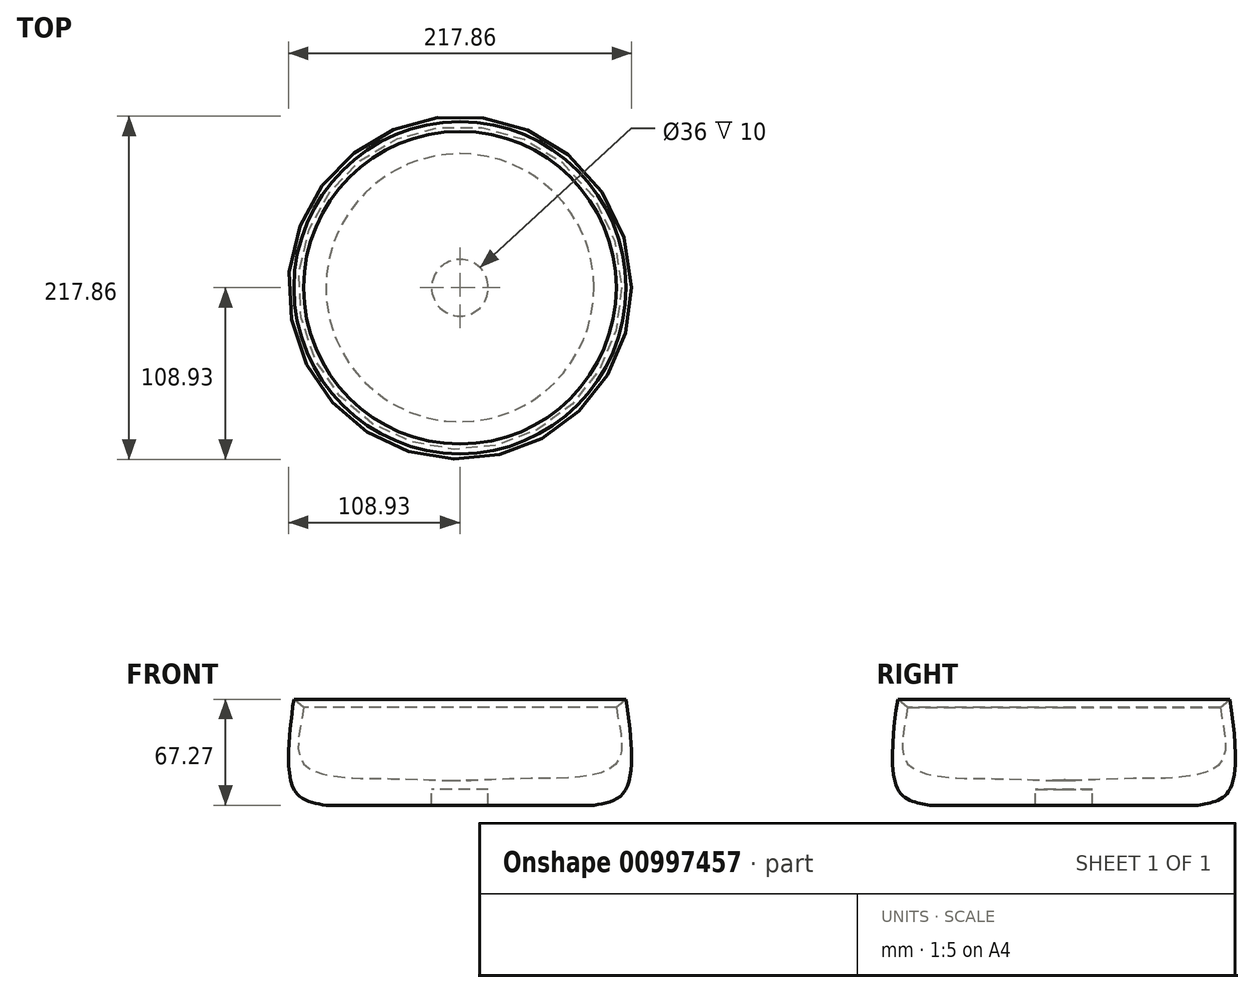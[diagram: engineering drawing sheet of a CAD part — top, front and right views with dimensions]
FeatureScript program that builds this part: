
annotation { "Feature Type Name" : "Feature", "Feature Type Description" : "" }
export const myFeature = defineFeature(function(context is Context, id is Id, definition is map)
    precondition{}
    {
        {
            var Q0;
            Q0=qCreatedBy(makeId("Front.planeOp"),FACE);
            var sketch = newSketch(context, id + "F0", { "sketchPlane" : qUnion([Q0])});
            skLineSegment(sketch, "E0.top", {"start": v(0, 10) * mm, "end": v(18, 10) * mm});
            skLineSegment(sketch, "E0.right", {"start": v(18, 0) * mm, "end": v(18, 10) * mm});
            skLineSegment(sketch, "E1", {"start": v(18, 0) * mm, "end": v(85.12, 0) * mm});
            skFitSpline(sketch, "E2", {"points": [v(85.12, 0) * mm, v(104.67, 8.92) * mm, v(105.46, 67.27) * mm], "startDerivative": vector(59.85, 10.55) * mm, "endDerivative": vector(-15.83, 104.7) * mm});
            skLineSegment(sketch, "E3", {"start": v(0, 16) * mm, "end": v(0, 10) * mm});
            skLineSegment(sketch, "E4", {"start": v(105.46, 67.27) * mm, "end": v(99.29, 62.18) * mm});
            skFitSpline(sketch, "E5", {"points": [v(99.29, 62.18) * mm, v(99.29, 26.49) * mm, v(39.52, 16.85) * mm, v(0, 16) * mm], "startDerivative": vector(15.04, -123.43) * mm, "endDerivative": vector(-113.7, 6.48) * mm});
            skSolve(sketch);
        }
        {
            var Q0;
            Q0=makeQuery(id+"F0.imprint","IMPRINT",FACE,{"disambiguationData":[TD([[makeQuery(id+"F0.imprint","IMPRINT",EDGE,{"derivedFrom":sQuery(id+"F0.wireOp",EDGE,"E0.top")}),1.0]])]});
            var Q1;
            Q1=sQuery(id+"F0.wireOp",EDGE,"E3");
            revolve(context, id + "F1", {"surfaceOperationType" : NewSurfaceOperationType.NEW, "entities" : qUnion([Q0]), "axis" : qUnion([Q1]), "revolveType" : RevolveType.FULL});
        }
    });
